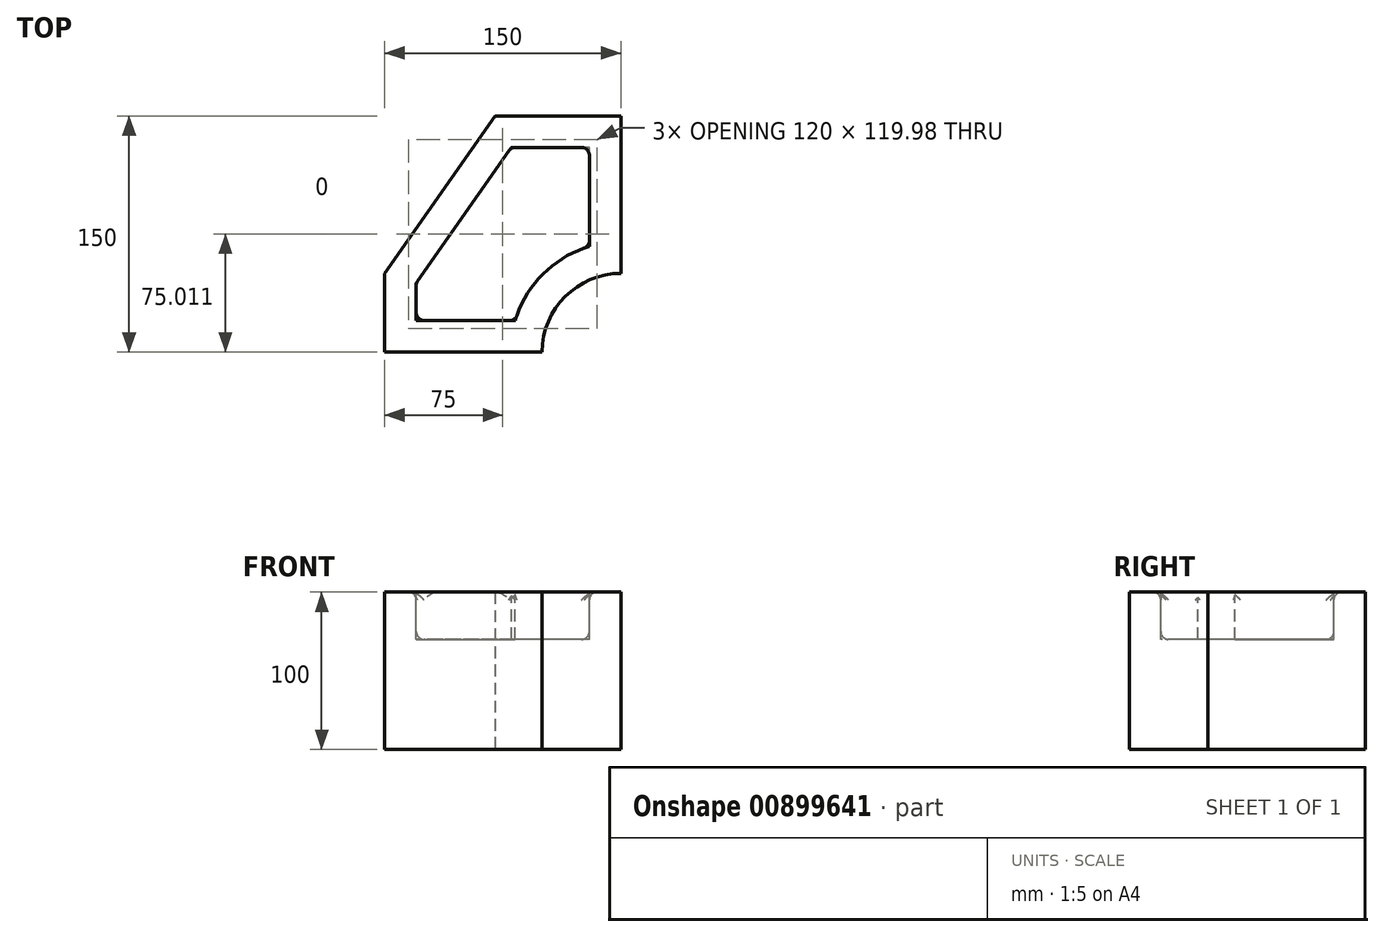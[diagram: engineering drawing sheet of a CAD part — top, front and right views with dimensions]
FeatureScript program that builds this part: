
annotation { "Feature Type Name" : "Feature", "Feature Type Description" : "" }
export const myFeature = defineFeature(function(context is Context, id is Id, definition is map)
    precondition{}
    {
        {
            var Q0;
            Q0=qCreatedBy(makeId("Top.planeOp"),FACE);
            var sketch = newSketch(context, id + "F0", { "sketchPlane" : qUnion([Q0])});
            skLineSegment(sketch, "E0", {"start": v(0, 0) * mm, "end": v(0, 50) * mm});
            skLineSegment(sketch, "E1", {"start": v(0, 50) * mm, "end": v(70, 150) * mm});
            skLineSegment(sketch, "E2", {"start": v(70, 150) * mm, "end": v(150, 150) * mm});
            skLineSegment(sketch, "E3", {"start": v(150, 150) * mm, "end": v(150, 50) * mm});
            skLineSegment(sketch, "E4", {"start": v(100, 0) * mm, "end": v(0, 0) * mm});
            skArc(sketch, "E5", {"start": v(150, 50) * mm, "mid": v(114.64, 35.36) * mm, "end": v(100, 0) * mm});
            skSolve(sketch);
        }
        {
            var Q0;
            Q0 = qSketchRegion(id + "F0", true);
            extrude(context, id + "F1", {"entities" : qUnion([Q0]), "depth" : 100 * mm, "offsetDistance" : 25 * mm});
        }
        {
            var Q0;
            Q0=makeQuery(id+"F1.opExtrude","CAP_FACE",FACE,{"disambiguationData":[OSD([sQuery(id+"F0.wireOp",EDGE,"E0"),sQuery(id+"F0.wireOp",EDGE,"E1"),sQuery(id+"F0.wireOp",EDGE,"E2"),sQuery(id+"F0.wireOp",EDGE,"E3"),sQuery(id+"F0.wireOp",EDGE,"E4"),sQuery(id+"F0.wireOp",EDGE,"E5")])],"isStart":false});
            var sketch = newSketch(context, id + "F2", { "sketchPlane" : qUnion([Q0])});
            skArc(sketch, "E6.0.0", {"start": v(100, 0) * mm, "mid": v(114.64, 35.36) * mm, "end": v(150, 50) * mm});
            skLineSegment(sketch, "E6.0.1", {"start": v(150, 50) * mm, "end": v(150, 150) * mm});
            skLineSegment(sketch, "E6.0.2", {"start": v(150, 150) * mm, "end": v(70, 150) * mm});
            skLineSegment(sketch, "E6.0.3", {"start": v(70, 150) * mm, "end": v(0, 50) * mm});
            skLineSegment(sketch, "E6.0.4", {"start": v(0, 50) * mm, "end": v(0, 0) * mm});
            skLineSegment(sketch, "E6.0.5", {"start": v(0, 0) * mm, "end": v(100, 0) * mm});
            skLineSegment(sketch, "E7.0", {"start": v(20, 20) * mm, "end": v(82.92, 20) * mm});
            skLineSegment(sketch, "E7.1", {"start": v(130, 67.08) * mm, "end": v(130, 130) * mm});
            skLineSegment(sketch, "E7.2", {"start": v(130, 130) * mm, "end": v(80.41, 130) * mm});
            skArc(sketch, "E7.3", {"start": v(82.92, 20) * mm, "mid": v(100.5, 49.5) * mm, "end": v(130, 67.08) * mm});
            skLineSegment(sketch, "E7.4", {"start": v(80.41, 130) * mm, "end": v(20, 43.7) * mm});
            skLineSegment(sketch, "E7.5", {"start": v(20, 43.7) * mm, "end": v(20, 20) * mm});
            skSolve(sketch);
        }
        {
            var Q0;
            Q0=makeQuery(id+"F2.imprint","IMPRINT",FACE,{"disambiguationData":[TD([[makeQuery(id+"F2.imprint","IMPRINT",EDGE,{"derivedFrom":sQuery(id+"F2.wireOp",EDGE,"E7.0")}),1.0]])]});
            var Q1;
            Q1=sQuery(id+"F2.wireOp",EDGE,"E7.5");
            var Q2;
            Q2=sQuery(id+"F2.wireOp",EDGE,"E7.4");
            var Q3;
            Q3=sQuery(id+"F2.wireOp",EDGE,"E7.2");
            var Q4;
            Q4=sQuery(id+"F2.wireOp",EDGE,"E7.1");
            var Q5;
            Q5=sQuery(id+"F2.wireOp",EDGE,"E7.3");
            var Q6;
            Q6=sQuery(id+"F2.wireOp",EDGE,"E7.0");
            extrude(context, id + "F3", {"entities" : qUnion([Q0]), "operationType" : NewBodyOperationType.REMOVE, "surfaceEntities" : qUnion([Q1, Q2, Q3, Q4, Q5, Q6]), "oppositeDirection" : true, "depth" : 30 * mm, "offsetDistance" : 25 * mm});
        }
        {
            var Q0;
            Q0=makeQuery(id+"F3.boolean.opBoolean","COPY",FACE,{"derivedFrom":makeQuery(id+"F3.opExtrude","CAP_FACE",FACE,{"disambiguationData":[OSD([sQuery(id+"F2.wireOp",EDGE,"E7.0"),sQuery(id+"F2.wireOp",EDGE,"E7.1"),sQuery(id+"F2.wireOp",EDGE,"E7.2"),sQuery(id+"F2.wireOp",EDGE,"E7.3"),sQuery(id+"F2.wireOp",EDGE,"E7.4"),sQuery(id+"F2.wireOp",EDGE,"E7.5")])],"isStart":false})});
            var Q1;
            Q1=makeQuery(id+"F3.boolean.opBoolean","COPY",FACE,{"derivedFrom":makeQuery(id+"F3.opExtrude","SWEPT_FACE",FACE,{"disambiguationData":[OSD([sQuery(id+"F2.wireOp",EDGE,"E7.4")])]})});
            var Q2;
            Q2=makeQuery(id+"F3.boolean.opBoolean","COPY",FACE,{"derivedFrom":makeQuery(id+"F3.opExtrude","SWEPT_FACE",FACE,{"disambiguationData":[OSD([sQuery(id+"F2.wireOp",EDGE,"E7.3")])]})});
            var Q3;
            Q3=makeQuery(id+"F3.boolean.opBoolean","COPY",FACE,{"derivedFrom":makeQuery(id+"F3.opExtrude","SWEPT_FACE",FACE,{"disambiguationData":[OSD([sQuery(id+"F2.wireOp",EDGE,"E7.5")])]})});
            var Q4;
            Q4=makeQuery(id+"F3.boolean.opBoolean","COPY",FACE,{"derivedFrom":makeQuery(id+"F3.opExtrude","SWEPT_FACE",FACE,{"disambiguationData":[OSD([sQuery(id+"F2.wireOp",EDGE,"E7.1")])]})});
            var Q5;
            Q5=makeQuery(id+"F3.boolean.opBoolean","COPY",FACE,{"derivedFrom":makeQuery(id+"F3.opExtrude","SWEPT_FACE",FACE,{"disambiguationData":[OSD([sQuery(id+"F2.wireOp",EDGE,"E7.2")])]})});
            fillet(context, id + "F4", {"entities" : qUnion([Q0, Q1, Q2, Q3, Q4, Q5]), "radius" : 5 * mm, "tangentPropagation" : true, "allowEdgeOverflow" : false});
        }
    });
